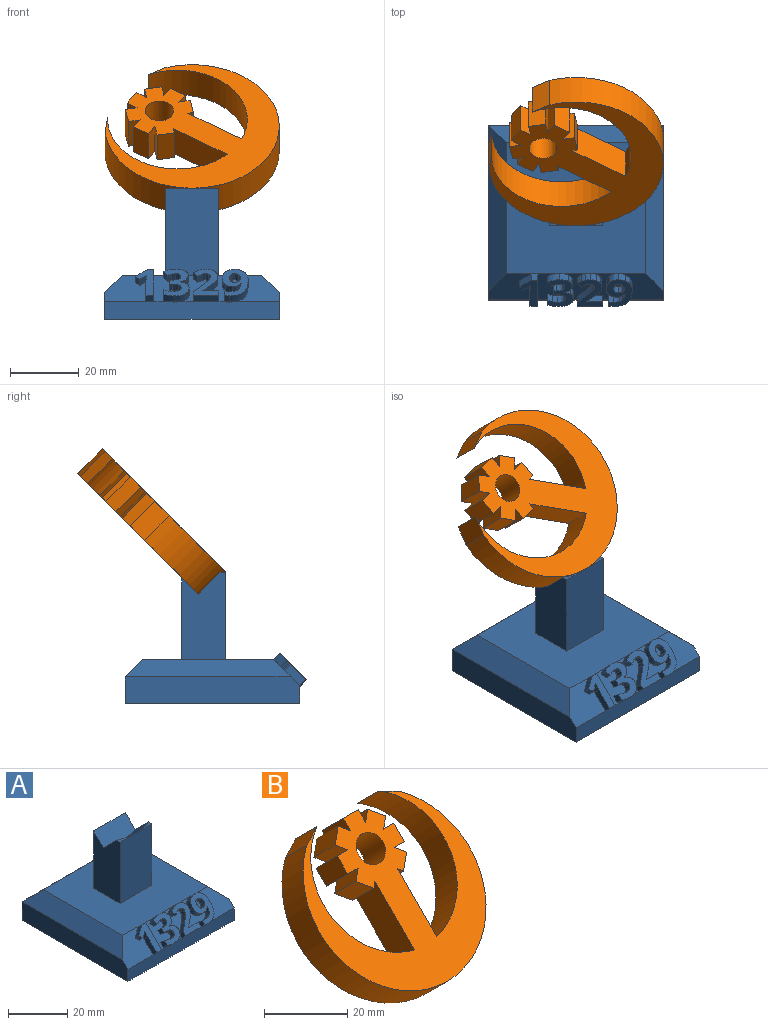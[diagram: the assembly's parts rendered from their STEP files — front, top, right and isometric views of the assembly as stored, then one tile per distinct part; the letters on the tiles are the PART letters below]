
ASSEMBLY  parts=2 mates=1
PART A: 118 faces, bbox 50.8x52.7x38.9 mm
  f0: plane 25.4x12.7mm, normal (-1,0,0), area 283.6mm2, adj f2,f8,f17,f18,f116,f117
  f1: plane 25.4x12.7mm, normal (1,0,0), area 283.6mm2, adj f3,f8,f17,f18,f116,f117
  f2: plane 7.62x1.65mm, normal (0,0,1), area 4.2mm2, adj f0,f18,f117
  f3: plane 7.62x1.65mm, normal (0,0,1), area 4.2mm2, adj f1,f18,f117
  f4: plane 12.98x7.74mm, normal (0,-0.71,0.71), area 87.5mm2, adj f8,f11,f12,f16,f94,f95,f96,f97
  f5: plane 11.07x7.64mm, normal (0,-0.71,0.71), area 40.5mm2, adj f8,f11,f74,f75,f76,f77,f78,f79
  f6: plane 9.11x7.7mm, normal (0,-0.71,0.71), area 44.5mm2, adj f8,f11,f31,f32,f33,f34,f35,f36
  f7: plane 22.23x7.68mm, normal (0,-0.71,0.71), area 166.4mm2, adj f8,f10,f11,f14,f19,f21,f22,f23
  f8: plane 40.64x38.1mm, normal (0,0,1), area 1354.8mm2, adj f0,f1,f4,f5,f6,f7,f14,f15
  f9: plane 50.8x7.62mm, normal (0,1,0), area 387.1mm2, adj f10,f12,f13,f15
  f10: plane 50.8x7.62mm, normal (-1,0,0), area 383.9mm2, adj f7,f9,f11,f13,f14
  f11: plane 50.8x5.08mm, normal (0,-1,0), area 258.1mm2, adj f4,f5,f6,f7,f10,f12,f13,f20
  f12: plane 50.8x7.62mm, normal (1,0,0), area 383.9mm2, adj f4,f9,f11,f13,f16
  f13: plane 50.8x50.8mm, normal (0,0,-1), area 2580.6mm2, adj f9,f10,f11,f12
  f14: plane 48.26x5.08mm, normal (-0.71,0,0.71), area 310.2mm2, adj f7,f8,f10,f15
  f15: plane 50.8x5.08mm, normal (0,0.71,0.71), area 328.5mm2, adj f8,f9,f14,f16
  f16: plane 48.26x5.08mm, normal (0.71,0,0.71), area 310.2mm2, adj f4,f8,f12,f15
  f17: plane 23.73x15.24mm, normal (0,1,0), area 361.7mm2, adj f0,f1,f8,f116
  f18: plane 25.4x15.24mm, normal (0,-1,0), area 387.1mm2, adj f0,f1,f2,f3,f8
  f19: plane 6.17x6.17mm, normal (-1,0,0), area 15.7mm2, adj f7,f20,f28,f29
  f20: plane 2.26x1.8mm, normal (0,-0.71,-0.71), area 5.7mm2, adj f11,f19,f21,f29
  f21: plane 9.35x9.35mm, normal (1,0,0), area 27.1mm2, adj f7,f20,f22,f29
  f22: plane 1.86x1.8mm, normal (0,0.71,0.71), area 4.7mm2, adj f7,f21,f23,f29
  f23: plane 3.73x3.73mm, normal (-0.62,0.55,0.55), area 11.2mm2, adj f7,f22,f24,f29
  f24: plane 2.76x2.76mm, normal (-0.78,-0.44,-0.44), area 4.4mm2, adj f7,f23,f25,f29
  f25: plane 2.49x2.49mm, normal (0.63,-0.55,-0.55), area 4mm2, adj f7,f24,f26,f29
  f26: extruded ~2.32x2.32mm, area 2.7mm2, adj f7,f25,f27,f29
  f27: plane 2.58x2.58mm, normal (-1,0.02,0.02), area 2.8mm2, adj f7,f26,f28,f29
  f28: plane 2.51x2.51mm, normal (-1,0.02,0.02), area 2.6mm2, adj f7,f19,f27,f29
  f29: plane 7.56x7.56mm, normal (0,-0.71,0.71), area 29.5mm2, adj f19,f20,f21,f22,f23,f24,f25,f26
  f30: plane 3.25x0.13mm, normal (0,0.71,-0.71), area 0.3mm2, adj f11,f31,f57
  f31: extruded ~3.19x2.4mm, area 8.5mm2, adj f6,f30,f32,f57,f58
  f32: extruded ~3.49x3.49mm, area 7mm2, adj f6,f31,f33,f58
  f33: extruded ~2.99x2.99mm, area 4.7mm2, adj f6,f32,f34,f58
  f34: extruded ~2.35x2.35mm, area 5.5mm2, adj f6,f33,f35,f58
  f35: plane 1.83x1.83mm, normal (1,0,0), area 0.1mm2, adj f6,f34,f36,f58
  f36: extruded ~2.48x2.48mm, area 5.1mm2, adj f6,f35,f37,f58
  f37: extruded ~3x3mm, area 4.7mm2, adj f6,f36,f38,f58
  f38: extruded ~3.12x3.12mm, area 5.6mm2, adj f6,f37,f39,f58
  f39: extruded ~2.62x2.27mm, area 7mm2, adj f6,f38,f40,f58,f59
  f40: extruded ~3.49x2.54mm, area 9.4mm2, adj f7,f39,f41,f58,f59
  f41: plane 2.9x2.9mm, normal (-0.83,-0.39,-0.39), area 4.8mm2, adj f7,f40,f42,f58
  f42: extruded ~2.22x2.22mm, area 3.4mm2, adj f7,f41,f43,f58
  f43: extruded ~1.92x1.92mm, area 2.8mm2, adj f7,f42,f44,f58
  f44: extruded ~2.65x2.65mm, area 5.6mm2, adj f7,f43,f45,f58
  f45: extruded ~2.58x2.58mm, area 3.4mm2, adj f7,f44,f46,f58
  f46: extruded ~2.03x2.03mm, area 4.7mm2, adj f7,f45,f47,f58
  f47: plane 1.8x1.8mm, normal (0,0.71,0.71), area 2.1mm2, adj f7,f46,f48,f58
  f48: plane 3.02x3.02mm, normal (-1,0,0), area 4.4mm2, adj f7,f47,f49,f58
  f49: plane 1.8x1.8mm, normal (0,-0.71,-0.71), area 2.1mm2, adj f7,f48,f50,f58
  f50: extruded ~2.02x2.02mm, area 5.1mm2, adj f7,f49,f51,f58
  f51: extruded ~2.55x2.55mm, area 3.3mm2, adj f7,f50,f52,f58
  f52: extruded ~2.66x2.66mm, area 3.5mm2, adj f7,f51,f53,f58
  f53: extruded ~2.06x2.06mm, area 4.4mm2, adj f7,f52,f54,f58
  f54: extruded ~1.94x1.94mm, area 3.8mm2, adj f7,f53,f55,f58
  f55: extruded ~2.16x2.16mm, area 3.7mm2, adj f7,f54,f56,f58
  f56: plane 3.16x3.16mm, normal (-1,0,0), area 4.9mm2, adj f7,f55,f57,f58
  f57: extruded ~3.08x2.2mm, area 8mm2, adj f7,f30,f31,f56,f58
  f58: plane 7.77x7.77mm, normal (0,-0.71,0.71), area 43.2mm2, adj f31,f32,f33,f34,f35,f36,f37,f38
  f59: plane 1.89x0.05mm, normal (0,0.71,-0.71), area 0.1mm2, adj f8,f39,f40
  f60: extruded ~1.9x1.9mm, area 3.5mm2, adj f6,f61,f83,f84,f85
  f61: extruded ~2.1x2.1mm, area 3.1mm2, adj f6,f60,f62,f84
  f62: extruded ~2.47x2.47mm, area 4.1mm2, adj f6,f61,f63,f84
  f63: plane 2.82x2.82mm, normal (-0.76,-0.46,-0.46), area 4.8mm2, adj f6,f62,f64,f84
  f64: extruded ~2.37x2.37mm, area 3.7mm2, adj f6,f63,f65,f84
  f65: extruded ~2x2mm, area 3.2mm2, adj f6,f64,f66,f84
  f66: extruded ~2.02x2.02mm, area 2.6mm2, adj f6,f65,f67,f84
  f67: extruded ~2.47x2.47mm, area 2.7mm2, adj f6,f66,f68,f84
  f68: extruded ~2.38x2.38mm, area 2.2mm2, adj f6,f67,f69,f84
  f69: extruded ~2.41x2.41mm, area 2.6mm2, adj f6,f68,f70,f84
  f70: extruded ~2.99x2.99mm, area 5.8mm2, adj f6,f69,f71,f84
  f71: plane 3.71x3.71mm, normal (-0.71,0.5,0.5), area 9.7mm2, adj f6,f70,f72,f84
  f72: plane 2.91x2.91mm, normal (-1,0,0), area 4mm2, adj f6,f71,f73,f84
  f73: plane 7.47x1.8mm, normal (0,-0.71,-0.71), area 19mm2, adj f11,f72,f74,f84
  f74: plane 3.14x3.14mm, normal (1,0,0), area 4.8mm2, adj f5,f73,f75,f84
  f75: plane 4.66x1.8mm, normal (0,0.71,0.71), area 11.8mm2, adj f5,f74,f76,f84
  f76: plane 1.87x1.87mm, normal (1,0,0), area 0.3mm2, adj f5,f75,f77,f84
  f77: plane 2.71x2.71mm, normal (0.69,-0.52,-0.52), area 4.8mm2, adj f5,f76,f78,f84
  f78: extruded ~3.17x3.17mm, area 6.9mm2, adj f5,f77,f79,f84
  f79: extruded ~2.73x2.73mm, area 4mm2, adj f5,f78,f80,f84
  f80: extruded ~2.78x2.78mm, area 3.6mm2, adj f5,f79,f81,f84
  f81: extruded ~2.86x2.86mm, area 4mm2, adj f5,f80,f82,f84
  f82: extruded ~2.52x2.52mm, area 4mm2, adj f5,f81,f83,f84
  f83: extruded ~2.05x2.05mm, area 4.6mm2, adj f5,f60,f82,f84,f85
  f84: plane 7.66x7.66mm, normal (0,-0.71,0.71), area 42.5mm2, adj f60,f61,f62,f63,f64,f65,f66,f67
  f85: plane 1.7x0.05mm, normal (0,0.71,-0.71), area 0.1mm2, adj f8,f60,f83
  f86: plane 1.15x0.03mm, normal (0,0.71,-0.71), area 0mm2, adj f8,f98,f99
  f87: extruded ~2.14x2.14mm, area 3.2mm2, adj f88,f112,f113,f115
  f88: extruded ~2.22x2.22mm, area 3.5mm2, adj f87,f89,f113,f115
  f89: extruded ~2.83x2.83mm, area 4mm2, adj f88,f90,f113,f115
  f90: extruded ~2.53x2.53mm, area 3mm2, adj f89,f91,f113,f115
  f91: extruded ~2.11x2.11mm, area 3.3mm2, adj f90,f92,f113,f115
  f92: extruded ~2.12x2.12mm, area 3.1mm2, adj f91,f93,f113,f115
  f93: extruded ~2.66x2.66mm, area 3.3mm2, adj f92,f112,f113,f115
  f94: extruded ~4.03x2.9mm, area 11.3mm2, adj f4,f95,f111,f113,f114
  f95: extruded ~5.13x5.13mm, area 12.7mm2, adj f4,f94,f96,f113
  f96: extruded ~3.58x3.58mm, area 6.6mm2, adj f4,f95,f97,f113
  f97: extruded ~2.94x2.94mm, area 5.4mm2, adj f4,f96,f98,f113
  f98: extruded ~2.19x2.19mm, area 5.5mm2, adj f4,f86,f97,f99,f113
  f99: extruded ~2.66x2.5mm, area 7.4mm2, adj f5,f86,f98,f100,f113
  f100: extruded ~3.72x3.72mm, area 7.5mm2, adj f5,f99,f101,f113
  f101: extruded ~3.55x3.55mm, area 6.8mm2, adj f5,f100,f102,f113
  f102: extruded ~2.43x2.43mm, area 6.2mm2, adj f5,f101,f103,f113
  f103: extruded ~1.99x1.99mm, area 3.6mm2, adj f5,f102,f104,f113
  f104: extruded ~2.48x2.48mm, area 3.5mm2, adj f5,f103,f105,f113
  f105: plane 1.8x1.8mm, normal (0,-0.71,-0.71), area 0.2mm2, adj f5,f104,f106,f113
  f106: extruded ~3.18x3.18mm, area 5.2mm2, adj f5,f105,f107,f113
  f107: extruded ~2.53x2.53mm, area 4mm2, adj f5,f106,f108,f113
  f108: extruded ~2.03x2.03mm, area 4.8mm2, adj f5,f107,f109,f113
  f109: extruded ~1.9x1.9mm, area 3.3mm2, adj f5,f108,f110,f113
  f110: plane 3.08x3.08mm, normal (-1,0,0), area 4.6mm2, adj f5,f109,f111,f113,f114
  f111: extruded ~1.87x1.87mm, area 3.7mm2, adj f94,f110,f113,f114
  f112: extruded ~2.78x2.78mm, area 3.7mm2, adj f87,f93,f113,f115
  f113: plane 7.75x7.75mm, normal (0,-0.71,0.71), area 48.7mm2, adj f87,f88,f89,f90,f91,f92,f93,f94
  f114: plane 2.99x0.12mm, normal (0,0.71,-0.71), area 0.3mm2, adj f11,f94,f110,f111
  f115: plane 3.11x2.51mm, normal (0,-0.71,0.71), area 8.9mm2, adj f87,f88,f89,f90,f91,f92,f93,f112
  f116: plane 15.24x5.52mm, normal (0,-0.71,0.71), area 113mm2, adj f0,f1,f17,f117
  f117: cylinder r=25.4mm len=15.24mm, axis (0,-0.71,0.71), area 151.2mm2, adj f0,f1,f2,f3,f116
PART B: 31 faces, bbox 50.8x41x41 mm
  f0: plane 8.93x8.93mm, normal (0.71,0.5,0.5), area 35.5mm2, adj f1,f27,f29,f30
  f1: plane 9.66x9.66mm, normal (-1,0,0), area 35.5mm2, adj f0,f2,f29,f30
  f2: plane 7.18x7.18mm, normal (0,0.71,0.71), area 51.6mm2, adj f1,f3,f29,f30
  f3: plane 9.66x9.66mm, normal (1,0,0), area 35.5mm2, adj f2,f4,f29,f30
  f4: plane 8.93x8.93mm, normal (-0.71,0.5,0.5), area 35.5mm2, adj f3,f5,f29,f30
  f5: plane 9.72x9.72mm, normal (0.71,0.5,0.5), area 51.6mm2, adj f4,f6,f29,f30
  f6: plane 8.93x8.93mm, normal (0.71,-0.5,-0.5), area 35.5mm2, adj f5,f7,f29,f30
  f7: plane 7.18x7.18mm, normal (0,0.71,0.71), area 35.5mm2, adj f6,f8,f29,f30
  f8: plane 10.78x10.78mm, normal (1,0,0), area 51.6mm2, adj f7,f9,f29,f30
  f9: plane 7.18x7.18mm, normal (0,-0.71,-0.71), area 35.5mm2, adj f8,f10,f29,f30
  f10: plane 8.93x8.93mm, normal (0.71,0.5,0.5), area 35.5mm2, adj f9,f11,f29,f30
  f11: plane 9.72x9.72mm, normal (0.71,-0.5,-0.5), area 51.6mm2, adj f10,f12,f29,f30
  f12: plane 8.04x8.04mm, normal (-0.71,-0.5,-0.5), area 17.3mm2, adj f11,f13,f29,f30
  f13: plane 20.56x20.56mm, normal (1,0,0), area 192.1mm2, adj f12,f14,f29,f30
  f14: cylinder r=20.32mm len=33.59mm, axis (0,-0.71,0.71), area 497.4mm2, adj f13,f15,f29,f30
  f15: plane 9.07x9.07mm, normal (0.44,0.63,0.63), area 61mm2, adj f14,f16,f29,f30
  f16: cylinder r=25.4mm len=50.8mm, axis (0,-0.71,0.71), area 1272.3mm2, adj f15,f17,f29,f30
  f17: plane 9.07x9.07mm, normal (-0.44,0.63,0.63), area 61mm2, adj f16,f18,f29,f30
  f18: cylinder r=20.32mm len=33.59mm, axis (0,-0.71,0.71), area 497.4mm2, adj f17,f19,f29,f30
  f19: plane 20.56x20.56mm, normal (-1,0,0), area 192.1mm2, adj f18,f20,f29,f30
  f20: plane 8.04x8.04mm, normal (0.71,-0.5,-0.5), area 17.3mm2, adj f19,f21,f29,f30
  f21: plane 9.72x9.72mm, normal (-0.71,-0.5,-0.5), area 51.6mm2, adj f20,f22,f29,f30
  f22: plane 8.93x8.93mm, normal (-0.71,0.5,0.5), area 35.5mm2, adj f21,f23,f29,f30
  f23: plane 7.18x7.18mm, normal (0,-0.71,-0.71), area 35.5mm2, adj f22,f24,f29,f30
  f24: plane 10.78x10.78mm, normal (-1,0,0), area 51.6mm2, adj f23,f25,f29,f30
  f25: plane 7.18x7.18mm, normal (0,0.71,0.71), area 35.5mm2, adj f24,f26,f29,f30
  f26: plane 8.93x8.93mm, normal (-0.71,-0.5,-0.5), area 35.5mm2, adj f25,f27,f29,f30
  f27: plane 9.72x9.72mm, normal (-0.71,0.5,0.5), area 51.6mm2, adj f0,f26,f29,f30
  f28: cylinder r=4.1mm len=12.98mm, axis (0,-0.71,0.71), area 261.6mm2, adj f29,f30
  f29: plane 50.8x33.85mm, normal (0,0.71,-0.71), area 1070.4mm2, adj f0,f1,f2,f3,f4,f5,f6,f7
  f30: plane 50.8x33.85mm, normal (0,-0.71,0.71), area 1070.4mm2, adj f0,f1,f2,f3,f4,f5,f6,f7
PLACE A t=(-27.81,26.34,0)mm fixed
PLACE B rot(axis=(0,-0.71,0.71),56.1deg) t=(13.93,40.24,13.94)mm
MATE revolute B.f16 <-> A.f117  axis (0,-0.71,0.71) through (-25.4,43.12,52.49)mm
